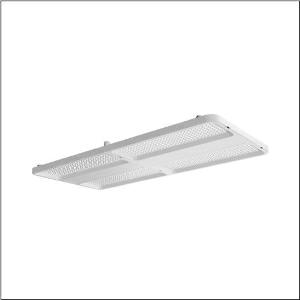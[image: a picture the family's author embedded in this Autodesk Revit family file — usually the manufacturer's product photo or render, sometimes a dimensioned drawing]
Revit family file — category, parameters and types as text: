
# Revit family: highbay_21_maxi_52hn11db3pda
name_source: partatom
category: Lighting Fixtures
units: mm (PartAtom-declared; Revit-internal decimal feet)

## family parameters
Cut with Voids When Loaded = No
Host = Face
Light Source = No
Part Type = Normal
Room Calculation Point = No
Round Connector Dimension = Use Diameter
Shared = No

## types (1)
- --- (1 x LED, 5350 lm, 31.4 W, 3000K)
    Apparent Load = 31 VA
    CIE Flux Codes = 89 97 99 100 100
    Color Rendering = 80
    Color Temperature = 3000K
    Default Elevation = 1800 mm
    Description = high bay luminaire Highbay 21 maxi; direct symmetric narrow distribution, light control with lens of PMMA; UGR ≤ 22 (X = 4H | Y = 8H | S = 0.25H | reflection values 70/50/20); luminous flux: 34.690lm; light colour: 830, colour temperature: 3000K, MacAdam ≤ 3 SDCM (initial), colour rendering: CRI > 80; luminous efficacy: 175,5lm/W; rated service life: 75.000h (L80) at AT= ta max; control: DALI 2; luminaire connection: terminal, 5-pole, max. 2.5mm² (cable entry for one cable, Ø 8.5..16mm); mains connection: 230..240V, AC/DC 0/50..60Hz; connected load: 197,7W; protection rating (complete): IP66; insulation class (complete): insulation class I (protective earthing); protection symbol: D; impact resistance: IK08; certification: CE, ENEC, VDE, UKCA; luminaire for central battery installations according to EN 60598-2-22, internal wiring halogen-free; luminaire LABS conformity tested according to VDMA 24364:2018-05; Suitable for use in the food industry according to the specifications of IFS-Food, HACCP and/or BRC; housing frame of high-performance plastic PA6, matt traffic white (RAL 9016); cover of PMMA; dimension (LxWxH): 946 x 442 x 72mm; permissible operating ambient temperature: -40..+60°C (reducing of maximum allowable ambient temperature of 5°C with ceiling mounting); packaging unit: 1 piece; (delivery without accessories; please order mounting accessories separately)
    Height = 72 mm  [stored 0.23622 ft]
    Lamp = 1 x LED
    Lamp Light Flux = 5350 lm
    Lamp Power = 31.4 W
    Lamp count = 1
    Length = 946 mm
    Luminous efficacy = 170 lm/W
    Manufacturer = Siteco
    ModVariant = No
    Model = 52HN11DB3PDA
    Mounting Place = Ceiling
    Mounting Type = Pendant
    Number of Poles = 1
    OnlyDefault = Yes
    Power Factor = 1
    Product Name = Highbay 21 maxi
    Product group = high bay luminaire
    ProductGroupID = 902
    Protection Class = Protection class I
    Protection Degree = IP 66
    RLX_Detail_Level = 1
    RLX_Emergency_Light_Flux = 0 lm
    RLX_Emergency_Type = 0
    RLX_Emergency_Type_DB = No
    RlxData = <blob elided: 128349 chars, md5=592aa2f9>
    Socket = socket
    Standby Power = 0 W
    System Light Flux = 5350 lm
    System Power = 31 W
    Type Comments = : DC mode (central or group accumulator) initial emergency light level
    Type Image = l_1363244.jpg
    URL = http://relux.com
    VarID = @adj_003303
    Voltage = 0 V
    Weight = 0.00 kg
    Width = 442 mm

note: [stored X ft] marks values corroborated as IEEE doubles in the binary element streams (Revit-internal decimal feet)

## geometry (parser evidence)
native form markers: Blend x4, Sweep x10
no freeform markers — native parametric forms only
